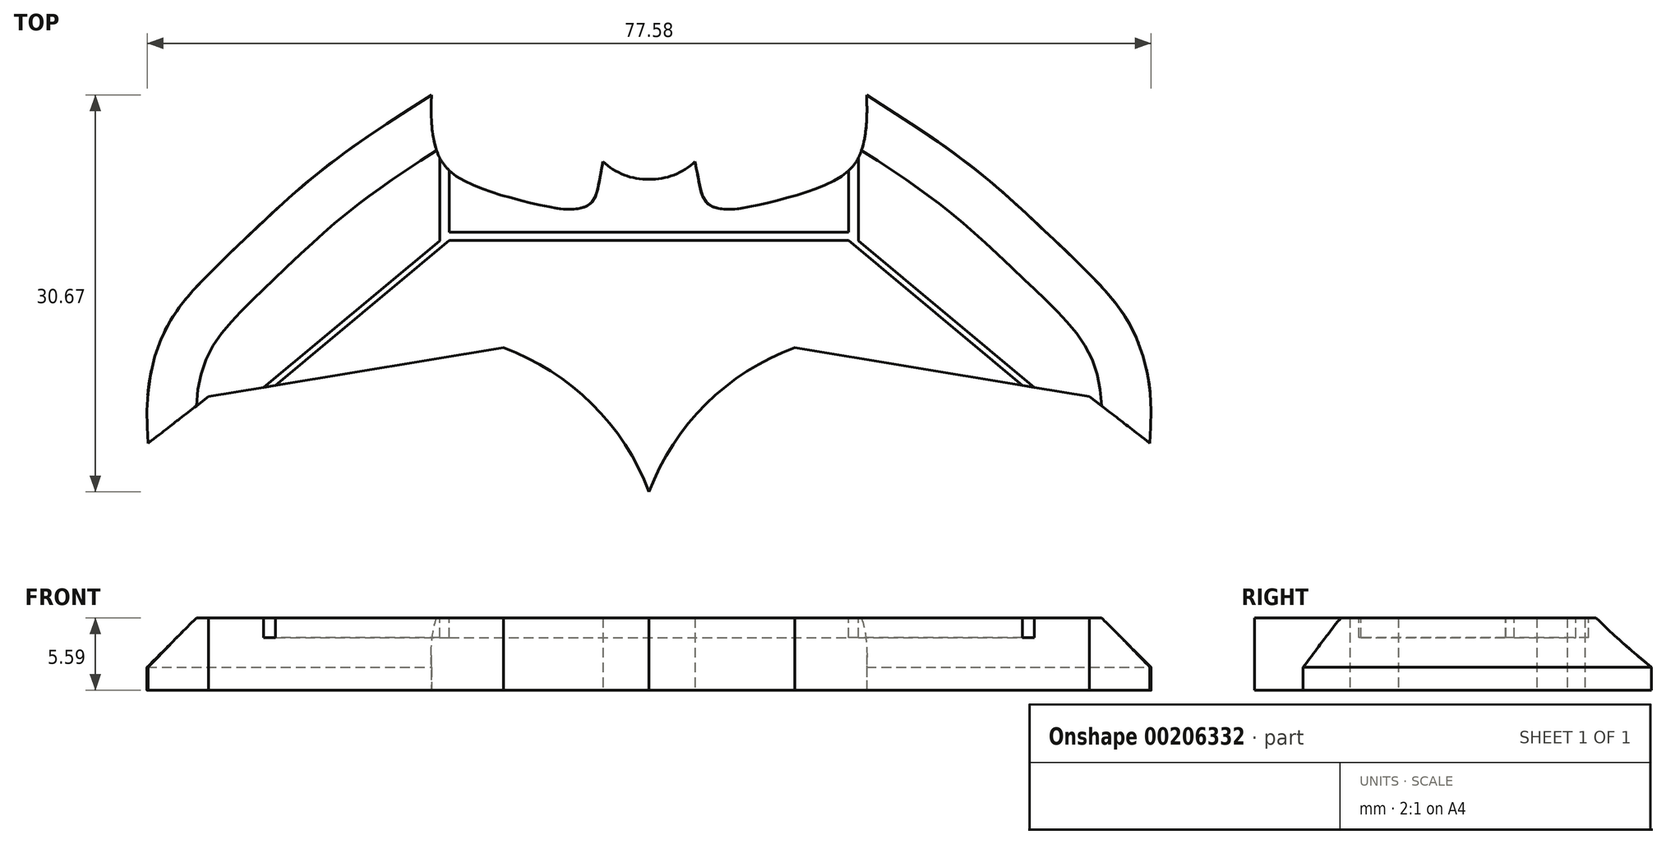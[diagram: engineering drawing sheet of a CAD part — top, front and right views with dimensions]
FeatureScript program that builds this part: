
annotation { "Feature Type Name" : "Feature", "Feature Type Description" : "" }
export const myFeature = defineFeature(function(context is Context, id is Id, definition is map)
    precondition{}
    {
        {
            var Q0;
            Q0=qCreatedBy(makeId("Top.planeOp"),FACE);
            var sketch = newSketch(context, id + "F0", { "sketchPlane" : qUnion([Q0])});
            skArc(sketch, "E0", {"start": v(16.8, -26.82) * mm, "mid": v(12.4, -20.02) * mm, "end": v(5.55, -15.7) * mm});
            skLineSegment(sketch, "E1", {"start": v(5.55, -15.7) * mm, "end": v(-17.23, -19.45) * mm});
            skLineSegment(sketch, "E2", {"start": v(-17.23, -19.45) * mm, "end": v(-21.9, -23.07) * mm});
            skFitSpline(sketch, "E3", {"points": [v(-21.9, -23.07) * mm, v(-21.9, -18.93) * mm, v(-20.34, -13.88) * mm, v(-16.97, -9.74) * mm, v(-13.6, -6.5) * mm, v(-8.17, -1.71) * mm, v(0, 3.85) * mm], "startDerivative": vector(-1.73, 28.9) * mm, "endDerivative": vector(39.9, 25.47) * mm});
            skFitSpline(sketch, "E4", {"points": [v(0, 3.85) * mm, v(0, 1.82) * mm, v(0.69, -1.11) * mm, v(2.68, -2.87) * mm, v(5.74, -3.99) * mm, v(8.85, -4.75) * mm, v(10.9, -4.98) * mm, v(12.37, -4.46) * mm, v(12.95, -2.87) * mm, v(13.25, -1.29) * mm], "startDerivative": vector(-0.66, -18.08) * mm, "endDerivative": vector(3.02, 16.48) * mm});
            skArc(sketch, "E5", {"start": v(13.25, -1.29) * mm, "mid": v(14.9, -2.33) * mm, "end": v(16.8, -2.67) * mm});
            skArc(sketch, "E6.MirrorCS", {"start": v(20.37, -1.29) * mm, "mid": v(18.73, -2.33) * mm, "end": v(16.8, -2.67) * mm});
            skArc(sketch, "E7.MirrorCS", {"start": v(16.8, -26.82) * mm, "mid": v(21.22, -20.02) * mm, "end": v(28.07, -15.7) * mm});
            skLineSegment(sketch, "E8.MirrorCS", {"start": v(28.07, -15.7) * mm, "end": v(50.85, -19.45) * mm});
            skLineSegment(sketch, "E9.MirrorCS", {"start": v(50.85, -19.45) * mm, "end": v(55.51, -23.07) * mm});
            skFitSpline(sketch, "E10.MirrorCS", {"points": [v(55.51, -23.07) * mm, v(55.51, -18.93) * mm, v(53.96, -13.88) * mm, v(50.6, -9.74) * mm, v(47.23, -6.5) * mm, v(41.8, -1.71) * mm, v(33.62, 3.85) * mm], "startDerivative": vector(1.73, 28.9) * mm, "endDerivative": vector(-39.9, 25.47) * mm});
            skFitSpline(sketch, "E11.MirrorCS", {"points": [v(33.62, 3.85) * mm, v(33.62, 1.82) * mm, v(32.93, -1.11) * mm, v(30.94, -2.87) * mm, v(27.88, -3.99) * mm, v(24.77, -4.75) * mm, v(22.72, -4.98) * mm, v(21.25, -4.46) * mm, v(20.66, -2.87) * mm, v(20.37, -1.29) * mm], "startDerivative": vector(0.66, -18.08) * mm, "endDerivative": vector(-3.02, 16.48) * mm});
            skSolve(sketch);
        }
        {
            var Q0;
            Q0=makeQuery(id+"F0.imprint","IMPRINT",FACE,{"disambiguationData":[TD([[makeQuery(id+"F0.imprint","IMPRINT",EDGE,{"derivedFrom":sQuery(id+"F0.wireOp",EDGE,"E0")}),-1.0]])]});
            extrude(context, id + "F1", {"entities" : qUnion([Q0]), "depth" : 5.6 * mm});
        }
        {
            var Q0;
            Q0=makeQuery(id+"F1.opExtrude","CAP_FACE",FACE,{"disambiguationData":[OSD([sQuery(id+"F0.wireOp",EDGE,"E0"),sQuery(id+"F0.wireOp",EDGE,"E1"),sQuery(id+"F0.wireOp",EDGE,"E2"),sQuery(id+"F0.wireOp",EDGE,"E3"),sQuery(id+"F0.wireOp",EDGE,"E4"),sQuery(id+"F0.wireOp",EDGE,"E5"),sQuery(id+"F0.wireOp",EDGE,"E6.MirrorCS"),sQuery(id+"F0.wireOp",EDGE,"E7.MirrorCS"),sQuery(id+"F0.wireOp",EDGE,"E8.MirrorCS"),sQuery(id+"F0.wireOp",EDGE,"E9.MirrorCS"),sQuery(id+"F0.wireOp",EDGE,"E10.MirrorCS"),sQuery(id+"F0.wireOp",EDGE,"E11.MirrorCS")])],"isStart":false});
            var sketch = newSketch(context, id + "F2", { "sketchPlane" : qUnion([Q0])});
            skLineSegment(sketch, "E12", {"start": v(0.63, -1) * mm, "end": v(0.63, -7.42) * mm});
            skLineSegment(sketch, "E13", {"start": v(0.63, -7.42) * mm, "end": v(-12.97, -18.74) * mm});
            skLineSegment(sketch, "E14", {"start": v(-12.05, -18.6) * mm, "end": v(1.38, -7.4) * mm});
            skLineSegment(sketch, "E15", {"start": v(1.38, -6.75) * mm, "end": v(1.38, -1.99) * mm});
            skLineSegment(sketch, "E16", {"start": v(16.8, -2.67) * mm, "end": v(16.8, -26.82) * mm});
            skLineSegment(sketch, "E17", {"start": v(1.38, -7.4) * mm, "end": v(16.8, -7.4) * mm});
            skLineSegment(sketch, "E18", {"start": v(1.38, -6.75) * mm, "end": v(16.8, -6.75) * mm});
            skLineSegment(sketch, "E19.MirrorCS", {"start": v(32.24, -6.75) * mm, "end": v(16.8, -6.75) * mm});
            skLineSegment(sketch, "E20.MirrorCS", {"start": v(32.24, -7.4) * mm, "end": v(16.8, -7.4) * mm});
            skLineSegment(sketch, "E21.MirrorCS", {"start": v(32.24, -6.75) * mm, "end": v(32.24, -1.99) * mm});
            skLineSegment(sketch, "E22.MirrorCS", {"start": v(33, -1) * mm, "end": v(33, -7.42) * mm});
            skLineSegment(sketch, "E23.MirrorCS", {"start": v(45.67, -18.6) * mm, "end": v(32.24, -7.4) * mm});
            skLineSegment(sketch, "E24.MirrorCS", {"start": v(33, -7.42) * mm, "end": v(46.6, -18.74) * mm});
            skSolve(sketch);
        }
        {
            var Q0;
            {var subQ4=sQuery(id+"F2.wireOp",EDGE,"E12");Q0=makeQuery(id+"F2.imprint","IMPRINT",FACE,{"disambiguationData":[TD([[makeQuery(id+"F2.imprint","IMPRINT",EDGE,{"derivedFrom":subQ4}),1.0]])]});}
            var Q1;
            {var subQ3=sQuery(id+"F2.wireOp",EDGE,"E19.MirrorCS");Q1=makeQuery(id+"F2.imprint","IMPRINT",FACE,{"disambiguationData":[TD([[makeQuery(id+"F2.imprint","IMPRINT",EDGE,{"derivedFrom":subQ3}),1.0]])]});}
            extrude(context, id + "F3", {"entities" : qUnion([Q0, Q1]), "operationType" : NewBodyOperationType.REMOVE, "oppositeDirection" : true, "depth" : 1.52 * mm});
        }
        {
            var Q0;
            Q0=makeQuery(id+"F1.opExtrude","CAP_EDGE",EDGE,{"disambiguationData":[OSD([sQuery(id+"F0.wireOp",EDGE,"E3")])],"isStart":false});
            var Q1;
            Q1=makeQuery(id+"F1.opExtrude","CAP_EDGE",EDGE,{"disambiguationData":[OSD([sQuery(id+"F0.wireOp",EDGE,"E10.MirrorCS")])],"isStart":false});
            chamfer(context, id + "F4", {"entities" : qUnion([Q0, Q1]), "width" : 3.8 * mm, "tangentPropagation" : true});
        }
    });
